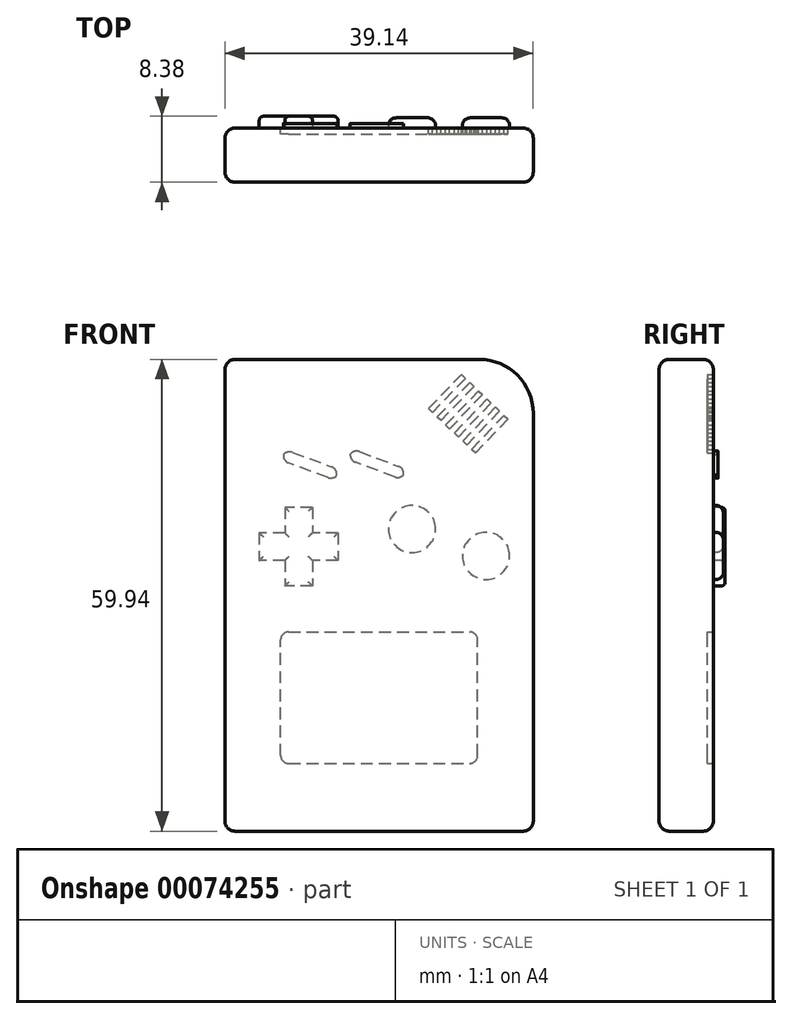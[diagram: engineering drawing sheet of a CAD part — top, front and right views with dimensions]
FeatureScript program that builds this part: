
annotation { "Feature Type Name" : "Feature", "Feature Type Description" : "" }
export const myFeature = defineFeature(function(context is Context, id is Id, definition is map)
    precondition{}
    {
        {
            var Q0;
            Q0=qCreatedBy(makeId("Front.planeOp"),FACE);
            var sketch = newSketch(context, id + "F0", { "sketchPlane" : qUnion([Q0])});
            skLineSegment(sketch, "E0.rect.bottom", {"start": v(-19.57, 29.97) * mm, "end": v(19.57, 29.97) * mm});
            skLineSegment(sketch, "E0.rect.top", {"start": v(-19.57, -29.97) * mm, "end": v(19.57, -29.97) * mm});
            skLineSegment(sketch, "E0.rect.left", {"start": v(-19.57, 29.97) * mm, "end": v(-19.57, -29.97) * mm});
            skLineSegment(sketch, "E0.rect.right", {"start": v(19.57, 29.97) * mm, "end": v(19.57, -29.97) * mm});
            skPoint(sketch, "E0.rect.middle", {"position": v(0, 0) * mm});
            skSolve(sketch);
        }
        {
            var Q0;
            Q0 = qSketchRegion(id + "F0", true);
            extrude(context, id + "F1", {"entities" : qUnion([Q0]), "oppositeDirection" : true, "depth" : 6.88 * mm});
        }
        {
            var Q0;
            Q0=makeQuery(id+"F1.opExtrude","SWEPT_EDGE",EDGE,{"disambiguationData":[OSD([sQuery(id+"F0.wireOp",EDGE,"E0.rect.bottom"),sQuery(id+"F0.wireOp",EDGE,"E0.rect.right")])]});
            fillet(context, id + "F2", {"entities" : qUnion([Q0]), "radius" : 6.86 * mm, "tangentPropagation" : true, "allowEdgeOverflow" : false});
        }
        {
            var Q0;
            Q0=makeQuery(id+"F1.opExtrude","CAP_EDGE",EDGE,{"disambiguationData":[OSD([sQuery(id+"F0.wireOp",EDGE,"E0.rect.bottom")])],"isStart":false});
            var Q1;
            Q1=makeQuery(id+"F1.opExtrude","SWEPT_EDGE",EDGE,{"disambiguationData":[OSD([sQuery(id+"F0.wireOp",EDGE,"E0.rect.bottom"),sQuery(id+"F0.wireOp",EDGE,"E0.rect.left")])]});
            var Q2;
            Q2=makeQuery(id+"F1.opExtrude","SWEPT_EDGE",EDGE,{"disambiguationData":[OSD([sQuery(id+"F0.wireOp",EDGE,"E0.rect.top"),sQuery(id+"F0.wireOp",EDGE,"E0.rect.left")])]});
            var Q3;
            Q3=makeQuery(id+"F1.opExtrude","CAP_EDGE",EDGE,{"disambiguationData":[OSD([sQuery(id+"F0.wireOp",EDGE,"E0.rect.left")])],"isStart":false});
            var Q4;
            Q4=makeQuery(id+"F1.opExtrude","CAP_EDGE",EDGE,{"disambiguationData":[OSD([sQuery(id+"F0.wireOp",EDGE,"E0.rect.left")])],"isStart":true});
            fillet(context, id + "F3", {"entities" : qUnion([Q0, Q1, Q2, Q3, Q4]), "radius" : 1.27 * mm, "tangentPropagation" : true, "allowEdgeOverflow" : false});
        }
        {
            var Q0;
            Q0=makeQuery(id+"F1.opExtrude","CAP_EDGE",EDGE,{"disambiguationData":[OSD([sQuery(id+"F0.wireOp",EDGE,"E0.rect.bottom")])],"isStart":true});
            var Q1;
            Q1=makeQuery(id+"F1.opExtrude","CAP_EDGE",EDGE,{"disambiguationData":[OSD([sQuery(id+"F0.wireOp",EDGE,"E0.rect.top")])],"isStart":false});
            var Q2;
            Q2=makeQuery(id+"F1.opExtrude","CAP_EDGE",EDGE,{"disambiguationData":[OSD([sQuery(id+"F0.wireOp",EDGE,"E0.rect.top")])],"isStart":true});
            fillet(context, id + "F4", {"entities" : qUnion([Q0, Q1, Q2]), "radius" : 1.27 * mm, "tangentPropagation" : true, "allowEdgeOverflow" : false});
        }
        {
            var Q0;
            Q0=qCreatedBy(makeId("Front.planeOp"),FACE);
            var sketch = newSketch(context, id + "F5", { "sketchPlane" : qUnion([Q0])});
            skCircle(sketch, "E1", {"center": v(13.57, 5) * mm, "radius": 3 * mm});
            skCircle(sketch, "E2", {"center": v(4.18, 8.42) * mm, "radius": 3 * mm});
            skLineSegment(sketch, "E3", {"start": v(4.18, 8.42) * mm, "end": v(13.57, 5) * mm, "construction": true});
            skSolve(sketch);
        }
        {
            var Q0;
            Q0 = qSketchRegion(id + "F5", true);
            extrude(context, id + "F6", {"entities" : qUnion([Q0]), "operationType" : NewBodyOperationType.ADD, "oppositeDirection" : true, "depth" : 8.2 * mm});
        }
        {
            var Q0;
            Q0=makeQuery(id+"F6.opExtrude","CAP_EDGE",EDGE,{"disambiguationData":[OSD([sQuery(id+"F5.wireOp",EDGE,"E2")])],"isStart":false});
            var Q1;
            Q1=makeQuery(id+"F6.opExtrude","CAP_FACE",FACE,{"disambiguationData":[OSD([sQuery(id+"F5.wireOp",EDGE,"E1")])],"isStart":false});
            fillet(context, id + "F7", {"entities" : qUnion([Q0, Q1]), "radius" : 1 * mm, "tangentPropagation" : true, "allowEdgeOverflow" : false});
        }
        {
            var Q0;
            Q0=makeQuery(id+"F1.opExtrude","CAP_FACE",FACE,{"disambiguationData":[OSD([sQuery(id+"F0.wireOp",EDGE,"E0.rect.bottom"),sQuery(id+"F0.wireOp",EDGE,"E0.rect.top"),sQuery(id+"F0.wireOp",EDGE,"E0.rect.left"),sQuery(id+"F0.wireOp",EDGE,"E0.rect.right")])],"isStart":false});
            var sketch = newSketch(context, id + "F8", { "sketchPlane" : qUnion([Q0])});
            skLineSegment(sketch, "E4.rect.bottom", {"start": v(8.48, 11.18) * mm, "end": v(11.98, 11.18) * mm});
            skLineSegment(sketch, "E4.rect.top", {"start": v(8.48, 1.18) * mm, "end": v(11.98, 1.18) * mm});
            skLineSegment(sketch, "E4.rect.left", {"start": v(8.48, 11.18) * mm, "end": v(8.48, 1.18) * mm});
            skLineSegment(sketch, "E4.rect.right", {"start": v(11.98, 11.18) * mm, "end": v(11.98, 1.18) * mm});
            skPoint(sketch, "E4.rect.middle", {"position": v(10.23, 6.18) * mm});
            skLineSegment(sketch, "E5.rect.bottom", {"start": v(5.23, 7.93) * mm, "end": v(15.23, 7.93) * mm});
            skLineSegment(sketch, "E5.rect.top", {"start": v(5.23, 4.43) * mm, "end": v(15.23, 4.43) * mm});
            skLineSegment(sketch, "E5.rect.left", {"start": v(5.23, 7.93) * mm, "end": v(5.23, 4.43) * mm});
            skLineSegment(sketch, "E5.rect.right", {"start": v(15.23, 7.93) * mm, "end": v(15.23, 4.43) * mm});
            skSolve(sketch);
        }
        {
            var Q0;
            Q0 = qSketchRegion(id + "F8", true);
            extrude(context, id + "F9", {"entities" : qUnion([Q0]), "operationType" : NewBodyOperationType.ADD, "depth" : 1.5 * mm});
        }
        {
            var Q0;
            Q0=makeQuery(id+"F9.opExtrude","CAP_FACE",FACE,{"disambiguationData":[OSD([sQuery(id+"F8.wireOp",EDGE,"E4.rect.bottom"),sQuery(id+"F8.wireOp",EDGE,"E4.rect.top"),sQuery(id+"F8.wireOp",EDGE,"E4.rect.left"),sQuery(id+"F8.wireOp",EDGE,"E4.rect.right"),sQuery(id+"F8.wireOp",EDGE,"E5.rect.bottom"),sQuery(id+"F8.wireOp",EDGE,"E5.rect.top"),sQuery(id+"F8.wireOp",EDGE,"E5.rect.left"),sQuery(id+"F8.wireOp",EDGE,"E5.rect.right")])],"isStart":false});
            fillet(context, id + "F10", {"entities" : qUnion([Q0]), "radius" : 0.5 * mm, "tangentPropagation" : true, "allowEdgeOverflow" : false});
        }
        {
            var Q0;
            Q0=makeQuery(id+"F1.opExtrude","CAP_FACE",FACE,{"disambiguationData":[OSD([sQuery(id+"F0.wireOp",EDGE,"E0.rect.bottom"),sQuery(id+"F0.wireOp",EDGE,"E0.rect.top"),sQuery(id+"F0.wireOp",EDGE,"E0.rect.left"),sQuery(id+"F0.wireOp",EDGE,"E0.rect.right")])],"isStart":false});
            var sketch = newSketch(context, id + "F11", { "sketchPlane" : qUnion([Q0])});
            skLineSegment(sketch, "E6.rect.bottom", {"start": v(12.51, -21.35) * mm, "end": v(-12.51, -21.35) * mm});
            skLineSegment(sketch, "E6.rect.top", {"start": v(12.51, -4.67) * mm, "end": v(-12.51, -4.67) * mm});
            skLineSegment(sketch, "E6.rect.left", {"start": v(12.51, -21.35) * mm, "end": v(12.51, -4.67) * mm});
            skLineSegment(sketch, "E6.rect.right", {"start": v(-12.51, -21.35) * mm, "end": v(-12.51, -4.67) * mm});
            skPoint(sketch, "E6.rect.middle", {"position": v(0, -13) * mm});
            skSolve(sketch);
        }
        {
            var Q0;
            Q0 = qSketchRegion(id + "F11", true);
            extrude(context, id + "F12", {"entities" : qUnion([Q0]), "operationType" : NewBodyOperationType.REMOVE, "oppositeDirection" : true, "depth" : 0.75 * mm});
        }
        {
            var Q0;
            Q0=makeQuery(id+"F1.opExtrude","CAP_FACE",FACE,{"disambiguationData":[OSD([sQuery(id+"F0.wireOp",EDGE,"E0.rect.bottom"),sQuery(id+"F0.wireOp",EDGE,"E0.rect.top"),sQuery(id+"F0.wireOp",EDGE,"E0.rect.left"),sQuery(id+"F0.wireOp",EDGE,"E0.rect.right")])],"isStart":false});
            var sketch = newSketch(context, id + "F13", { "sketchPlane" : qUnion([Q0])});
            skLineSegment(sketch, "E7", {"start": v(-16.37, 22.39) * mm, "end": v(-12.22, 18.05) * mm});
            skLineSegment(sketch, "E8", {"start": v(-12.22, 18.05) * mm, "end": v(-11.72, 18.54) * mm});
            skLineSegment(sketch, "E9", {"start": v(-11.72, 18.54) * mm, "end": v(-15.87, 22.87) * mm});
            skLineSegment(sketch, "E10", {"start": v(-15.87, 22.87) * mm, "end": v(-16.37, 22.39) * mm});
            skLineSegment(sketch, "E11", {"start": v(-15.87, 22.87) * mm, "end": v(-4.54, 22.63) * mm, "construction": true});
            skPoint(sketch, "E11.endSnap0", {"position": v(-16.12, 22.63) * mm});
            skLineSegment(sketch, "E12.0.1.0", {"start": v(-10.63, 19.57) * mm, "end": v(-14.78, 23.9) * mm});
            skPoint(sketch, "E12.0.1.1", {"position": v(-15.03, 23.66) * mm});
            skLineSegment(sketch, "E12.0.1.2", {"start": v(-15.28, 23.42) * mm, "end": v(-11.13, 19.09) * mm});
            skLineSegment(sketch, "E12.0.1.3", {"start": v(-11.13, 19.09) * mm, "end": v(-10.63, 19.57) * mm});
            skLineSegment(sketch, "E12.0.1.4", {"start": v(-14.78, 23.9) * mm, "end": v(-15.28, 23.42) * mm});
            skLineSegment(sketch, "E12.0.1.5", {"start": v(-14.78, 23.9) * mm, "end": v(-3.45, 23.66) * mm, "construction": true});
            skLineSegment(sketch, "E12.0.2.0", {"start": v(-9.54, 20.6) * mm, "end": v(-13.7, 24.94) * mm});
            skPoint(sketch, "E12.0.2.1", {"position": v(-13.95, 24.7) * mm});
            skLineSegment(sketch, "E12.0.2.2", {"start": v(-14.2, 24.45) * mm, "end": v(-10.05, 20.12) * mm});
            skLineSegment(sketch, "E12.0.2.3", {"start": v(-10.05, 20.12) * mm, "end": v(-9.54, 20.6) * mm});
            skLineSegment(sketch, "E12.0.2.4", {"start": v(-13.7, 24.94) * mm, "end": v(-14.2, 24.45) * mm});
            skLineSegment(sketch, "E12.0.2.5", {"start": v(-13.7, 24.94) * mm, "end": v(-2.36, 24.7) * mm, "construction": true});
            skLineSegment(sketch, "E12.0.3.0", {"start": v(-8.45, 21.64) * mm, "end": v(-12.6, 25.97) * mm});
            skPoint(sketch, "E12.0.3.1", {"position": v(-12.86, 25.73) * mm});
            skLineSegment(sketch, "E12.0.3.2", {"start": v(-13.11, 25.49) * mm, "end": v(-8.96, 21.16) * mm});
            skLineSegment(sketch, "E12.0.3.3", {"start": v(-8.96, 21.16) * mm, "end": v(-8.45, 21.64) * mm});
            skLineSegment(sketch, "E12.0.3.4", {"start": v(-12.6, 25.97) * mm, "end": v(-13.11, 25.49) * mm});
            skLineSegment(sketch, "E12.0.3.5", {"start": v(-12.6, 25.97) * mm, "end": v(-1.28, 25.73) * mm, "construction": true});
            skLineSegment(sketch, "E12.0.4.0", {"start": v(-7.37, 22.67) * mm, "end": v(-11.52, 27) * mm});
            skPoint(sketch, "E12.0.4.1", {"position": v(-11.77, 26.76) * mm});
            skLineSegment(sketch, "E12.0.4.2", {"start": v(-12.02, 26.52) * mm, "end": v(-7.87, 22.19) * mm});
            skLineSegment(sketch, "E12.0.4.3", {"start": v(-7.87, 22.19) * mm, "end": v(-7.37, 22.67) * mm});
            skLineSegment(sketch, "E12.0.4.4", {"start": v(-11.52, 27) * mm, "end": v(-12.02, 26.52) * mm});
            skLineSegment(sketch, "E12.0.4.5", {"start": v(-11.52, 27) * mm, "end": v(-0.19, 26.76) * mm, "construction": true});
            skLineSegment(sketch, "E12.0.5.0", {"start": v(-6.28, 23.7) * mm, "end": v(-10.43, 28.04) * mm});
            skPoint(sketch, "E12.0.5.1", {"position": v(-10.68, 27.8) * mm});
            skLineSegment(sketch, "E12.0.5.2", {"start": v(-10.94, 27.56) * mm, "end": v(-6.79, 23.22) * mm});
            skLineSegment(sketch, "E12.0.5.3", {"start": v(-6.79, 23.22) * mm, "end": v(-6.28, 23.7) * mm});
            skLineSegment(sketch, "E12.0.5.4", {"start": v(-10.43, 28.04) * mm, "end": v(-10.94, 27.56) * mm});
            skLineSegment(sketch, "E12.0.5.5", {"start": v(-10.43, 28.04) * mm, "end": v(0.9, 27.8) * mm, "construction": true});
            skLineSegment(sketch, "E12.direction1", {"start": v(-12.22, 18.05) * mm, "end": v(12.78, 18.05) * mm, "construction": true});
            skLineSegment(sketch, "E12.direction2", {"start": v(-12.22, 18.05) * mm, "end": v(-11.13, 19.09) * mm, "construction": true});
            skSolve(sketch);
        }
        {
            var Q0;
            Q0 = qSketchRegion(id + "F13", true);
            var Q1;
            Q1=makeQuery(id+"F13.imprint","IMPRINT",FACE,{"disambiguationData":[TD([[makeQuery(id+"F13.imprint","IMPRINT",EDGE,{"derivedFrom":sQuery(id+"F13.wireOp",EDGE,"E12.0.4.0")}),1.0]])]});
            extrude(context, id + "F14", {"entities" : qUnion([Q0, Q1]), "operationType" : NewBodyOperationType.REMOVE, "oppositeDirection" : true, "depth" : 0.77 * mm});
        }
        {
            var Q0;
            Q0=makeQuery(id+"F1.opExtrude","CAP_FACE",FACE,{"disambiguationData":[OSD([sQuery(id+"F0.wireOp",EDGE,"E0.rect.bottom"),sQuery(id+"F0.wireOp",EDGE,"E0.rect.top"),sQuery(id+"F0.wireOp",EDGE,"E0.rect.left"),sQuery(id+"F0.wireOp",EDGE,"E0.rect.right")])],"isStart":false});
            var sketch = newSketch(context, id + "F15", { "sketchPlane" : qUnion([Q0])});
            skLineSegment(sketch, "E13", {"start": v(5.63, 14.64) * mm, "end": v(12.46, 17.18) * mm});
            skLineSegment(sketch, "E14", {"start": v(12.46, 17.18) * mm, "end": v(11.96, 18.52) * mm});
            skLineSegment(sketch, "E15", {"start": v(11.96, 18.52) * mm, "end": v(4.98, 15.92) * mm});
            skLineSegment(sketch, "E16", {"start": v(4.98, 15.92) * mm, "end": v(5.63, 14.64) * mm});
            skLineSegment(sketch, "E17.1.0.0", {"start": v(-2.87, 14.72) * mm, "end": v(3.96, 17.26) * mm});
            skLineSegment(sketch, "E17.1.0.1", {"start": v(3.96, 17.26) * mm, "end": v(3.46, 18.6) * mm});
            skLineSegment(sketch, "E17.1.0.2", {"start": v(3.46, 18.6) * mm, "end": v(-3.52, 16) * mm});
            skLineSegment(sketch, "E17.1.0.3", {"start": v(-3.52, 16) * mm, "end": v(-2.87, 14.72) * mm});
            skLineSegment(sketch, "E17.direction1", {"start": v(4.98, 15.92) * mm, "end": v(-3.52, 16) * mm, "construction": true});
            skSolve(sketch);
        }
        {
            var Q0;
            Q0=makeQuery(id+"F15.imprint","IMPRINT",FACE,{"disambiguationData":[TD([[makeQuery(id+"F15.imprint","IMPRINT",EDGE,{"derivedFrom":sQuery(id+"F15.wireOp",EDGE,"E13")}),1.0]])]});
            extrude(context, id + "F16", {"entities" : qUnion([Q0]), "operationType" : NewBodyOperationType.ADD, "depth" : 0.6 * mm});
        }
        {
            var Q0;
            Q0 = qSketchRegion(id + "F15", true);
            extrude(context, id + "F17", {"entities" : qUnion([Q0]), "operationType" : NewBodyOperationType.ADD, "depth" : 0.6 * mm});
        }
        {
            var Q0;
            Q0=makeQuery(id+"F16.opExtrude","SWEPT_EDGE",EDGE,{"disambiguationData":[OSD([sQuery(id+"F15.wireOp",EDGE,"E13"),sQuery(id+"F15.wireOp",EDGE,"E16")])]});
            var Q1;
            Q1=makeQuery(id+"F16.opExtrude","SWEPT_EDGE",EDGE,{"disambiguationData":[OSD([sQuery(id+"F15.wireOp",EDGE,"E13"),sQuery(id+"F15.wireOp",EDGE,"E14")])]});
            var Q2;
            Q2=makeQuery(id+"F16.opExtrude","SWEPT_EDGE",EDGE,{"disambiguationData":[OSD([sQuery(id+"F15.wireOp",EDGE,"E15"),sQuery(id+"F15.wireOp",EDGE,"E16")])]});
            var Q3;
            Q3=makeQuery(id+"F16.opExtrude","SWEPT_EDGE",EDGE,{"disambiguationData":[OSD([sQuery(id+"F15.wireOp",EDGE,"E14"),sQuery(id+"F15.wireOp",EDGE,"E15")])]});
            fillet(context, id + "F18", {"entities" : qUnion([Q0, Q1, Q2, Q3]), "radius" : 1 * mm, "tangentPropagation" : true, "allowEdgeOverflow" : false});
        }
        {
            var Q0;
            Q0=makeQuery(id+"F17.opExtrude","SWEPT_EDGE",EDGE,{"disambiguationData":[OSD([sQuery(id+"F15.wireOp",EDGE,"E17.1.0.1"),sQuery(id+"F15.wireOp",EDGE,"E17.1.0.2")])]});
            var Q1;
            Q1=makeQuery(id+"F17.opExtrude","SWEPT_EDGE",EDGE,{"disambiguationData":[OSD([sQuery(id+"F15.wireOp",EDGE,"E17.1.0.2"),sQuery(id+"F15.wireOp",EDGE,"E17.1.0.3")])]});
            var Q2;
            Q2=makeQuery(id+"F17.opExtrude","SWEPT_EDGE",EDGE,{"disambiguationData":[OSD([sQuery(id+"F15.wireOp",EDGE,"E17.1.0.0"),sQuery(id+"F15.wireOp",EDGE,"E17.1.0.1")])]});
            var Q3;
            Q3=makeQuery(id+"F17.opExtrude","SWEPT_EDGE",EDGE,{"disambiguationData":[OSD([sQuery(id+"F15.wireOp",EDGE,"E17.1.0.0"),sQuery(id+"F15.wireOp",EDGE,"E17.1.0.3")])]});
            fillet(context, id + "F19", {"entities" : qUnion([Q0, Q1, Q2, Q3]), "radius" : 1 * mm, "tangentPropagation" : true, "allowEdgeOverflow" : false});
        }
        {
            var Q0;
            Q0=makeQuery(id+"F12.boolean.opBoolean","COPY",EDGE,{"derivedFrom":makeQuery(id+"F12.opExtrude","SWEPT_EDGE",EDGE,{"disambiguationData":[OSD([sQuery(id+"F11.wireOp",EDGE,"E6.rect.bottom"),sQuery(id+"F11.wireOp",EDGE,"E6.rect.right")])]})});
            fillet(context, id + "F20", {"entities" : qUnion([Q0]), "radius" : 1 * mm, "tangentPropagation" : true, "allowEdgeOverflow" : false});
        }
        {
            var Q0;
            Q0=makeQuery(id+"F12.boolean.opBoolean","COPY",EDGE,{"derivedFrom":makeQuery(id+"F12.opExtrude","SWEPT_EDGE",EDGE,{"disambiguationData":[OSD([sQuery(id+"F11.wireOp",EDGE,"E6.rect.top"),sQuery(id+"F11.wireOp",EDGE,"E6.rect.right")])]})});
            fillet(context, id + "F21", {"entities" : qUnion([Q0]), "radius" : 1 * mm, "tangentPropagation" : true, "allowEdgeOverflow" : false});
        }
        {
            var Q0;
            Q0=makeQuery(id+"F12.boolean.opBoolean","COPY",EDGE,{"derivedFrom":makeQuery(id+"F12.opExtrude","SWEPT_EDGE",EDGE,{"disambiguationData":[OSD([sQuery(id+"F11.wireOp",EDGE,"E6.rect.top"),sQuery(id+"F11.wireOp",EDGE,"E6.rect.left")])]})});
            var Q1;
            Q1=makeQuery(id+"F12.boolean.opBoolean","COPY",EDGE,{"derivedFrom":makeQuery(id+"F12.opExtrude","SWEPT_EDGE",EDGE,{"disambiguationData":[OSD([sQuery(id+"F11.wireOp",EDGE,"E6.rect.bottom"),sQuery(id+"F11.wireOp",EDGE,"E6.rect.left")])]})});
            fillet(context, id + "F22", {"entities" : qUnion([Q0, Q1]), "radius" : 1 * mm, "tangentPropagation" : true, "allowEdgeOverflow" : false});
        }
    });
